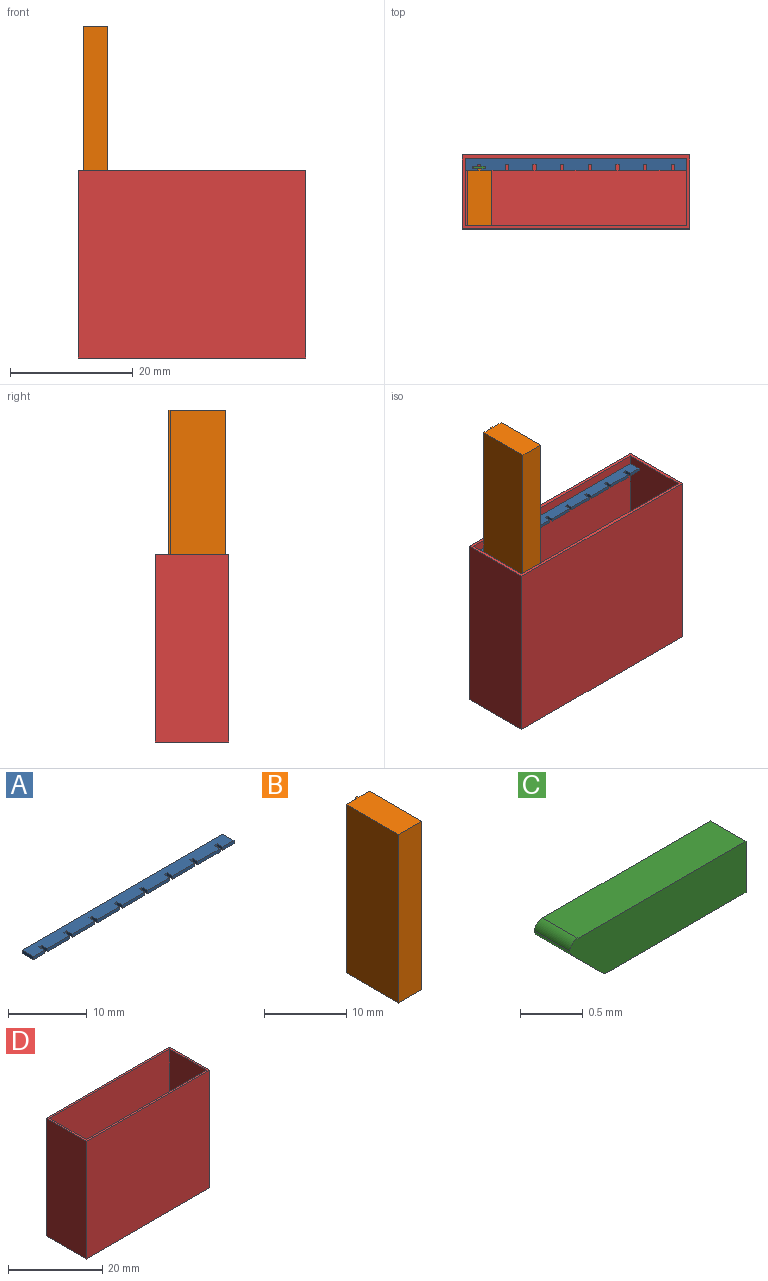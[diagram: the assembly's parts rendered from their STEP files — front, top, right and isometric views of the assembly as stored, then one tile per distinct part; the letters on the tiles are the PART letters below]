
ASSEMBLY  parts=4 mates=3
PART A: 38 faces, bbox 36x2x0.5 mm
  f0: plane 1x0.5mm, normal (-1,0,0), area 0.5mm2, adj f1,f35,f36,f37
  f1: plane 2x0.5mm, normal (0,-1,0), area 1mm2, adj f0,f2,f36,f37
  f2: plane 2x0.5mm, normal (1,0,0), area 1mm2, adj f1,f3,f36,f37
  f3: plane 36x0.5mm, normal (0,1,0), area 18mm2, adj f2,f4,f36,f37
  f4: plane 2x0.5mm, normal (-1,0,0), area 1mm2, adj f3,f5,f36,f37
  f5: plane 2x0.5mm, normal (0,-1,0), area 1mm2, adj f4,f6,f36,f37
  f6: plane 1x0.5mm, normal (1,0,0), area 0.5mm2, adj f5,f7,f36,f37
  f7: plane 0.5x0.5mm, normal (0,-1,0), area 0.3mm2, adj f6,f8,f36,f37
  f8: plane 1x0.5mm, normal (-1,0,0), area 0.5mm2, adj f7,f9,f36,f37
  f9: plane 4x0.5mm, normal (0,-1,0), area 2mm2, adj f8,f10,f36,f37
  f10: plane 1x0.5mm, normal (1,0,0), area 0.5mm2, adj f9,f11,f36,f37
  f11: plane 0.5x0.5mm, normal (0,-1,0), area 0.3mm2, adj f10,f12,f36,f37
  f12: plane 1x0.5mm, normal (-1,0,0), area 0.5mm2, adj f11,f13,f36,f37
  f13: plane 4x0.5mm, normal (0,-1,0), area 2mm2, adj f12,f14,f36,f37
  f14: plane 1x0.5mm, normal (1,0,0), area 0.5mm2, adj f13,f15,f36,f37
  f15: plane 0.5x0.5mm, normal (0,-1,0), area 0.3mm2, adj f14,f16,f36,f37
  f16: plane 1x0.5mm, normal (-1,0,0), area 0.5mm2, adj f15,f17,f36,f37
  f17: plane 4x0.5mm, normal (0,-1,0), area 2mm2, adj f16,f18,f36,f37
  f18: plane 1x0.5mm, normal (1,0,0), area 0.5mm2, adj f17,f19,f36,f37
  f19: plane 0.5x0.5mm, normal (0,-1,0), area 0.3mm2, adj f18,f20,f36,f37
  f20: plane 1x0.5mm, normal (-1,0,0), area 0.5mm2, adj f19,f21,f36,f37
  f21: plane 4x0.5mm, normal (0,-1,0), area 2mm2, adj f20,f22,f36,f37
  f22: plane 1x0.5mm, normal (1,0,0), area 0.5mm2, adj f21,f23,f36,f37
  f23: plane 0.5x0.5mm, normal (0,-1,0), area 0.3mm2, adj f22,f24,f36,f37
  f24: plane 1x0.5mm, normal (-1,0,0), area 0.5mm2, adj f23,f25,f36,f37
  f25: plane 4x0.5mm, normal (0,-1,0), area 2mm2, adj f24,f26,f36,f37
  f26: plane 1x0.5mm, normal (1,0,0), area 0.5mm2, adj f25,f27,f36,f37
  f27: plane 0.5x0.5mm, normal (0,-1,0), area 0.3mm2, adj f26,f28,f36,f37
  f28: plane 1x0.5mm, normal (-1,0,0), area 0.5mm2, adj f27,f29,f36,f37
  f29: plane 4x0.5mm, normal (0,-1,0), area 2mm2, adj f28,f30,f36,f37
  f30: plane 1x0.5mm, normal (1,0,0), area 0.5mm2, adj f29,f31,f36,f37
  f31: plane 0.5x0.5mm, normal (0,-1,0), area 0.3mm2, adj f30,f32,f36,f37
  f32: plane 1x0.5mm, normal (-1,0,0), area 0.5mm2, adj f31,f33,f36,f37
  f33: plane 4x0.5mm, normal (0,-1,0), area 2mm2, adj f32,f34,f36,f37
  f34: plane 1x0.5mm, normal (1,0,0), area 0.5mm2, adj f33,f35,f36,f37
  f35: plane 0.5x0.5mm, normal (0,-1,0), area 0.3mm2, adj f0,f34,f36,f37
  f36: plane 36x2mm, normal (0,0,1), area 68mm2, adj f0,f1,f2,f3,f4,f5,f6,f7
  f37: plane 36x2mm, normal (0,0,-1), area 68mm2, adj f0,f1,f2,f3,f4,f5,f6,f7
PART B: 10 faces, bbox 4x9.3x25 mm
  f0: plane 25x0.25mm, normal (-1,0,0), area 6.3mm2, adj f1,f7,f8,f9
  f1: plane 25x1.8mm, normal (0,1,0), area 45mm2, adj f0,f2,f8,f9
  f2: plane 25x9mm, normal (-1,0,0), area 225mm2, adj f1,f3,f8,f9
  f3: plane 25x4mm, normal (0,-1,0), area 100mm2, adj f2,f4,f8,f9
  f4: plane 25x9mm, normal (1,0,0), area 225mm2, adj f3,f5,f8,f9
  f5: plane 25x1.8mm, normal (0,1,0), area 45mm2, adj f4,f6,f8,f9
  f6: plane 25x0.25mm, normal (1,0,0), area 6.3mm2, adj f5,f7,f8,f9
  f7: plane 25x0.4mm, normal (0,1,0), area 10mm2, adj f0,f6,f8,f9
  f8: plane 9.25x4mm, normal (0,0,1), area 36.1mm2, adj f0,f1,f2,f3,f4,f5,f6,f7
  f9: plane 9.25x4mm, normal (0,0,-1), area 36.1mm2, adj f0,f1,f2,f3,f4,f5,f6,f7
PART C: 9 faces, bbox 2x0.4x0.5 mm
  f0: plane 2x0.5mm, normal (0,1,0), area 0.9mm2, adj f2,f3,f4,f5,f6,f7,f8
  f1: plane 2x0.5mm, normal (0,-1,0), area 0.9mm2, adj f2,f3,f4,f5,f6,f7,f8
  f2: plane 0.5x0.4mm, normal (1,0,0), area 0.2mm2, adj f0,f1,f3,f4
  f3: plane 1.9x0.4mm, normal (0,0,1), area 0.8mm2, adj f0,f1,f2,f7
  f4: plane 1.56x0.4mm, normal (0,0,-1), area 0.6mm2, adj f0,f1,f2,f6
  f5: plane 0.4x0.34mm, normal (-0.71,0,-0.71), area 0.2mm2, adj f0,f1,f6,f8
  f6: cylinder r=0.1mm len=0.4mm, axis (0,1,0), area 0mm2, adj f0,f1,f4,f5
  f7: cylinder r=0.1mm len=0.4mm, axis (0,1,0), area 0.1mm2, adj f0,f1,f3,f8
  f8: cylinder r=0.1mm len=0.4mm, axis (0,-1,0), area 0mm2, adj f0,f1,f5,f7
PART D: 51 faces, bbox 37x12x30.5 mm
  f0: plane 37x30.5mm, normal (0,1,0), area 1128.5mm2, adj f1,f7,f8,f9
  f1: plane 30.5x12mm, normal (-1,0,0), area 366mm2, adj f0,f2,f8,f9
  f2: plane 37x30.5mm, normal (0,-1,0), area 1128.5mm2, adj f1,f7,f8,f9
  f3: plane 30x11mm, normal (1,0,0), area 330mm2, adj f4,f6,f8,f10
  f4: plane 36x30mm, normal (0,-1,0), area 1080mm2, adj f3,f5,f8,f10
  f5: plane 30x11mm, normal (-1,0,0), area 330mm2, adj f4,f6,f8,f10
  f6: plane 36x30mm, normal (0,1,0), area 1080mm2, adj f3,f5,f8,f10
  f7: plane 30.5x12mm, normal (1,0,0), area 366mm2, adj f0,f2,f8,f9
  f8: plane 37x12mm, normal (0,0,1), area 48mm2, adj f0,f1,f2,f3,f4,f5,f6,f7
  f9: plane 37x12mm, normal (0,0,-1), area 444mm2, adj f0,f1,f2,f7
  f10: plane 36x11mm, normal (0,0,1), area 392mm2, adj f3,f4,f5,f6,f12,f13,f14,f15
  f11: plane 1x0.5mm, normal (0,0,1), area 0.5mm2, adj f12,f13,f14,f15
  f12: plane 1x0.5mm, normal (0,1,0), area 0.5mm2, adj f10,f11,f13,f15
  f13: plane 1x1mm, normal (1,0,0), area 1mm2, adj f10,f11,f12,f14
  f14: plane 1x0.5mm, normal (0,-1,0), area 0.5mm2, adj f10,f11,f13,f15
  f15: plane 1x1mm, normal (-1,0,0), area 1mm2, adj f10,f11,f12,f14
  f16: plane 1x0.5mm, normal (0,0,1), area 0.5mm2, adj f17,f18,f19,f20
  f17: plane 1x0.5mm, normal (0,1,0), area 0.5mm2, adj f10,f16,f18,f20
  f18: plane 1x1mm, normal (1,0,0), area 1mm2, adj f10,f16,f17,f19
  f19: plane 1x0.5mm, normal (0,-1,0), area 0.5mm2, adj f10,f16,f18,f20
  f20: plane 1x1mm, normal (-1,0,0), area 1mm2, adj f10,f16,f17,f19
  f21: plane 1x0.5mm, normal (0,0,1), area 0.5mm2, adj f22,f23,f24,f25
  f22: plane 1x0.5mm, normal (0,1,0), area 0.5mm2, adj f10,f21,f23,f25
  f23: plane 1x1mm, normal (1,0,0), area 1mm2, adj f10,f21,f22,f24
  f24: plane 1x0.5mm, normal (0,-1,0), area 0.5mm2, adj f10,f21,f23,f25
  f25: plane 1x1mm, normal (-1,0,0), area 1mm2, adj f10,f21,f22,f24
  f26: plane 1x0.5mm, normal (0,0,1), area 0.5mm2, adj f27,f28,f29,f30
  f27: plane 1x0.5mm, normal (0,1,0), area 0.5mm2, adj f10,f26,f28,f30
  f28: plane 1x1mm, normal (1,0,0), area 1mm2, adj f10,f26,f27,f29
  f29: plane 1x0.5mm, normal (0,-1,0), area 0.5mm2, adj f10,f26,f28,f30
  f30: plane 1x1mm, normal (-1,0,0), area 1mm2, adj f10,f26,f27,f29
  f31: plane 1x0.5mm, normal (0,0,1), area 0.5mm2, adj f32,f33,f34,f35
  f32: plane 1x0.5mm, normal (0,1,0), area 0.5mm2, adj f10,f31,f33,f35
  f33: plane 1x1mm, normal (1,0,0), area 1mm2, adj f10,f31,f32,f34
  f34: plane 1x0.5mm, normal (0,-1,0), area 0.5mm2, adj f10,f31,f33,f35
  f35: plane 1x1mm, normal (-1,0,0), area 1mm2, adj f10,f31,f32,f34
  f36: plane 1x0.5mm, normal (0,0,1), area 0.5mm2, adj f37,f38,f39,f40
  f37: plane 1x0.5mm, normal (0,1,0), area 0.5mm2, adj f10,f36,f38,f40
  f38: plane 1x1mm, normal (1,0,0), area 1mm2, adj f10,f36,f37,f39
  f39: plane 1x0.5mm, normal (0,-1,0), area 0.5mm2, adj f10,f36,f38,f40
  f40: plane 1x1mm, normal (-1,0,0), area 1mm2, adj f10,f36,f37,f39
  f41: plane 1x0.5mm, normal (0,0,1), area 0.5mm2, adj f42,f43,f44,f45
  f42: plane 1x0.5mm, normal (0,1,0), area 0.5mm2, adj f10,f41,f43,f45
  f43: plane 1x1mm, normal (1,0,0), area 1mm2, adj f10,f41,f42,f44
  f44: plane 1x0.5mm, normal (0,-1,0), area 0.5mm2, adj f10,f41,f43,f45
  f45: plane 1x1mm, normal (-1,0,0), area 1mm2, adj f10,f41,f42,f44
  f46: plane 1x0.5mm, normal (0,1,0), area 0.4mm2, adj f10,f47,f49,f50
  f47: plane 1x1mm, normal (1,0,0), area 1mm2, adj f10,f46,f48,f50
  f48: plane 1x0.5mm, normal (0,-1,0), area 0.5mm2, adj f10,f47,f49,f50
  f49: plane 1x0.8mm, normal (-1,0,0), area 0.8mm2, adj f10,f46,f48,f50
  f50: plane 1x0.5mm, normal (-0.37,0,0.93), area 0.5mm2, adj f46,f47,f48,f49
PLACE A t=(-55.21,46.95,28.5)mm
PLACE B t=(-59.5,31.71,29)mm
PLACE C t=(-71.33,36.55,28.99)mm
PLACE D t=(-55.21,46.95,0.5)mm
MATE revolute C.f1 <-> B.f7  axis (0,-1,0) through (-15.7,3.75,29.25)mm
MATE slider A.f37 <-> D.f10  axis (0,0,-1) through (-18,5.5,28.5)mm
MATE slider B.f9 <-> A.f36  axis (0,0,-1) through (-15.5,3.5,29)mm
